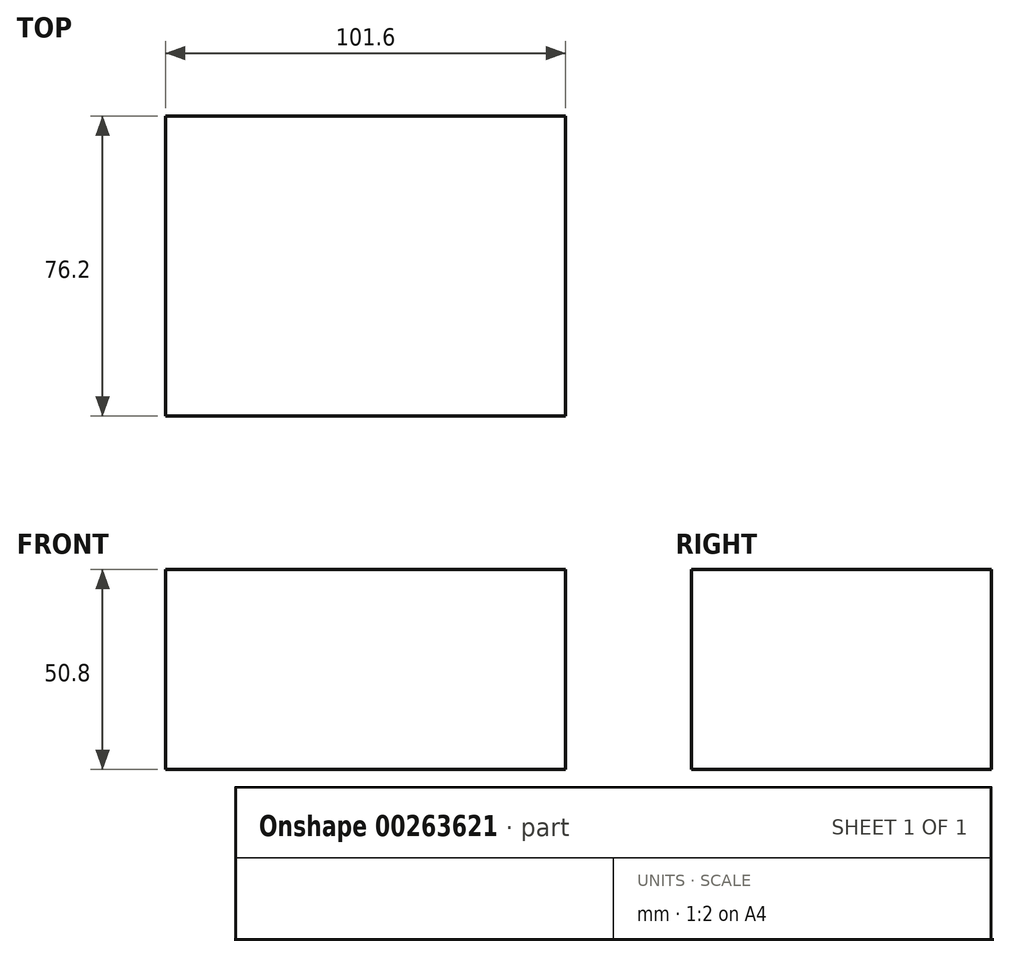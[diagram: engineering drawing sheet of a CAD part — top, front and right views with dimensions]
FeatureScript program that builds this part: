
annotation { "Feature Type Name" : "Feature", "Feature Type Description" : "" }
export const myFeature = defineFeature(function(context is Context, id is Id, definition is map)
    precondition{}
    {
        {
            var Q0;
            Q0=qCreatedBy(makeId("Front.planeOp"),FACE);
            var sketch = newSketch(context, id + "F0", { "sketchPlane" : qUnion([Q0])});
            skLineSegment(sketch, "E0", {"start": v(-75.34, 0) * mm, "end": v(-75.34, 50.8) * mm});
            skLineSegment(sketch, "E1", {"start": v(-75.34, 50.8) * mm, "end": v(26.26, 50.8) * mm});
            skLineSegment(sketch, "E2", {"start": v(26.26, 50.8) * mm, "end": v(26.26, 0) * mm});
            skLineSegment(sketch, "E3", {"start": v(26.26, 0) * mm, "end": v(-75.34, 0) * mm});
            skSolve(sketch);
        }
        {
            var Q0;
            Q0 = qSketchRegion(id + "F0", true);
            extrude(context, id + "F1", {"entities" : qUnion([Q0]), "depth" : 76.2 * mm});
        }
    });
